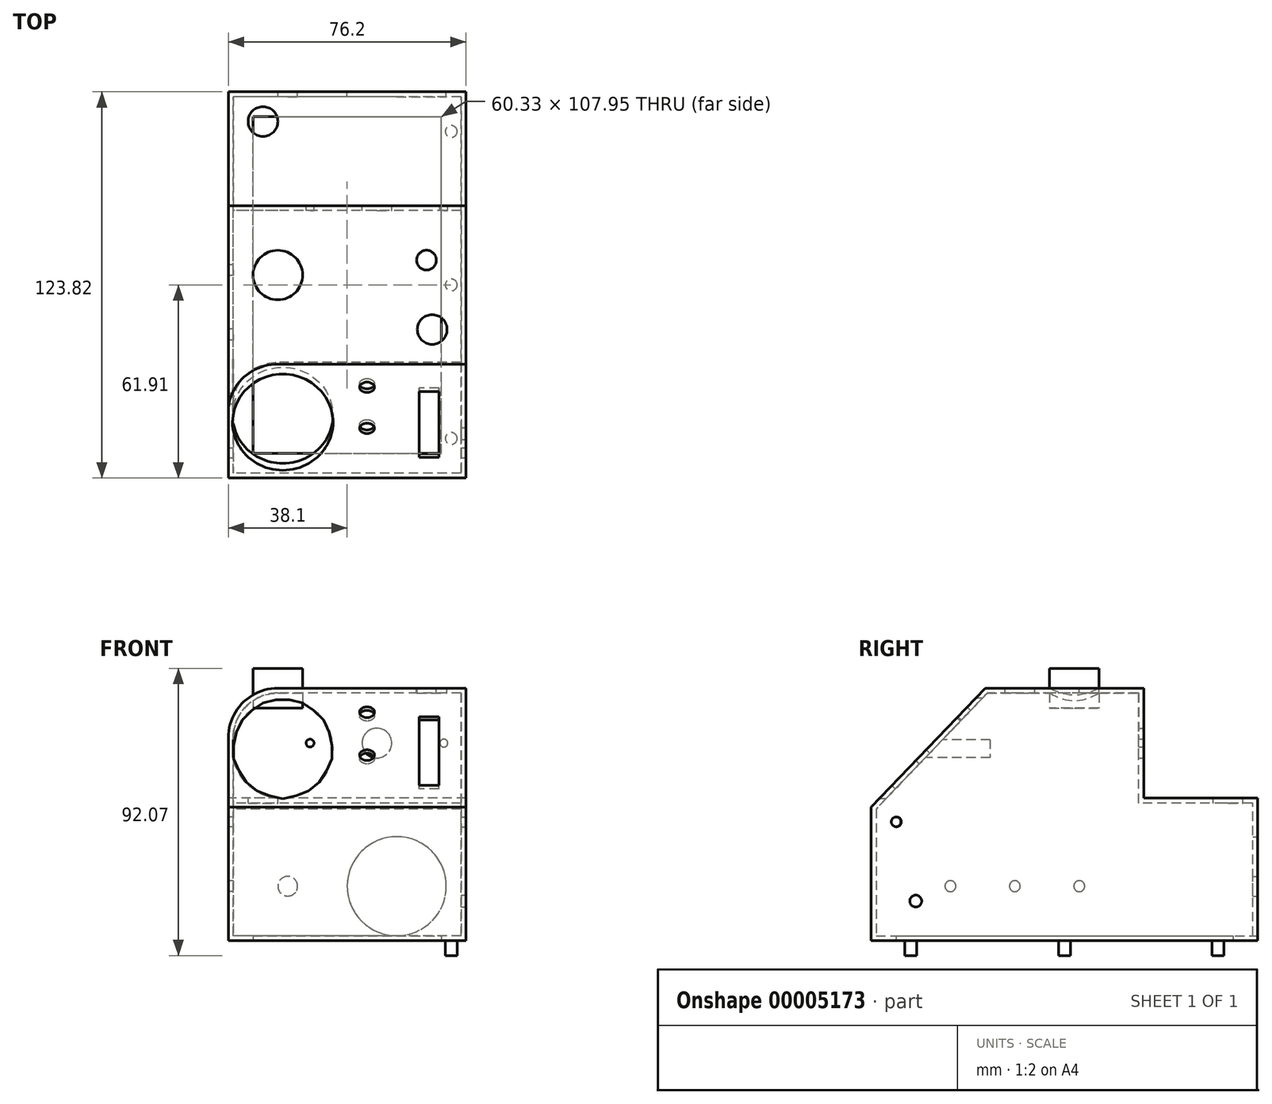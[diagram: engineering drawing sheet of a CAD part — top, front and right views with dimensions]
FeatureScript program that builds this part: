
annotation { "Feature Type Name" : "Feature", "Feature Type Description" : "" }
export const myFeature = defineFeature(function(context is Context, id is Id, definition is map)
    precondition{}
    {
        {
            var Q0;
            Q0=qCreatedBy(makeId("Right.planeOp"),FACE);
            var sketch = newSketch(context, id + "F0", { "sketchPlane" : qUnion([Q0])});
            skLineSegment(sketch, "E0", {"start": v(-61.91, -42.86) * mm, "end": v(61.91, -42.86) * mm});
            skLineSegment(sketch, "E1", {"start": v(61.91, -42.86) * mm, "end": v(61.91, 7.62) * mm});
            skLineSegment(sketch, "E2", {"start": v(61.91, 7.62) * mm, "end": v(25.4, 7.62) * mm});
            skLineSegment(sketch, "E3", {"start": v(25.4, 7.62) * mm, "end": v(25.4, 42.86) * mm});
            skLineSegment(sketch, "E4", {"start": v(25.4, 42.86) * mm, "end": v(-25.4, 42.86) * mm});
            skLineSegment(sketch, "E5", {"start": v(-25.4, 42.86) * mm, "end": v(-61.91, 4.76) * mm});
            skLineSegment(sketch, "E6", {"start": v(-61.91, 4.76) * mm, "end": v(-61.91, -42.86) * mm});
            skLineSegment(sketch, "E7", {"start": v(0, -42.86) * mm, "end": v(0, 42.86) * mm});
            skSolve(sketch);
        }
        {
            var Q0;
            {var subQ5=sQuery(id+"F0.wireOp",EDGE,"E5");var subQ9=sQuery(id+"F0.wireOp",EDGE,"E1");Q0=qUnion([makeQuery(id+"F0.imprint","IMPRINT",FACE,{"disambiguationData":[TD([[makeQuery(id+"F0.imprint","IMPRINT",EDGE,{"derivedFrom":subQ5}),1.0]])]}),makeQuery(id+"F0.imprint","IMPRINT",FACE,{"disambiguationData":[TD([[makeQuery(id+"F0.imprint","IMPRINT",EDGE,{"derivedFrom":subQ9}),1.0]])]})]);}
            extrude(context, id + "F1", {"entities" : qUnion([Q0]), "depth" : 76.2 * mm, "symmetric" : true});
        }
        {
            var Q0;
            Q0=makeQuery(id+"F1.opExtrude","CAP_EDGE",EDGE,{"disambiguationData":[OSD([sQuery(id+"F0.wireOp",EDGE,"E4")])],"isStart":true});
            fillet(context, id + "F2", {"entities" : qUnion([Q0]), "radius" : 15.88 * mm, "tangentPropagation" : true, "allowEdgeOverflow" : false});
        }
        {
            var Q0;
            Q0=makeQuery(id+"F1.opExtrude","SWEPT_FACE",FACE,{"disambiguationData":[OSD([sQuery(id+"F0.wireOp",EDGE,"E0")])]});
            shell(context, id + "F3", {"entities" : qUnion([Q0]), "thickness" : 1.59 * mm});
        }
        {
            var Q0;
            Q0=makeQuery(id+"F1.opExtrude","CAP_FACE",FACE,{"disambiguationData":[OSD([sQuery(id+"F0.wireOp",EDGE,"E0"),sQuery(id+"F0.wireOp",EDGE,"E1"),sQuery(id+"F0.wireOp",EDGE,"E2"),sQuery(id+"F0.wireOp",EDGE,"E3"),sQuery(id+"F0.wireOp",EDGE,"E4"),sQuery(id+"F0.wireOp",EDGE,"E5"),sQuery(id+"F0.wireOp",EDGE,"E6")])],"isStart":true});
            var sketch = newSketch(context, id + "F4", { "sketchPlane" : qUnion([Q0])});
            skCircle(sketch, "E8", {"center": v(36.51, -20.64) * mm, "radius": 1.75 * mm});
            skCircle(sketch, "E9", {"center": v(15.87, -20.64) * mm, "radius": 1.75 * mm});
            skCircle(sketch, "E10", {"center": v(-4.76, -20.64) * mm, "radius": 1.75 * mm});
            skCircle(sketch, "E11", {"center": v(53.97, 0) * mm, "radius": 1.59 * mm});
            skSolve(sketch);
        }
        {
            var Q0;
            {Q0=qUnion([makeQuery(id+"F4.imprint","IMPRINT",FACE,{"disambiguationData":[TD([[makeQuery(id+"F4.imprint","IMPRINT",EDGE,{"derivedFrom":sQuery(id+"F4.wireOp",EDGE,"E8")}),1.0]])]}),makeQuery(id+"F4.imprint","IMPRINT",FACE,{"disambiguationData":[TD([[makeQuery(id+"F4.imprint","IMPRINT",EDGE,{"derivedFrom":sQuery(id+"F4.wireOp",EDGE,"E9")}),1.0]])]}),makeQuery(id+"F4.imprint","IMPRINT",FACE,{"disambiguationData":[TD([[makeQuery(id+"F4.imprint","IMPRINT",EDGE,{"derivedFrom":sQuery(id+"F4.wireOp",EDGE,"E10")}),1.0]])]}),makeQuery(id+"F4.imprint","IMPRINT",FACE,{"disambiguationData":[TD([[makeQuery(id+"F4.imprint","IMPRINT",EDGE,{"derivedFrom":sQuery(id+"F4.wireOp",EDGE,"E11")}),1.0]])]})]);}
            extrude(context, id + "F5", {"entities" : qUnion([Q0]), "operationType" : NewBodyOperationType.REMOVE, "oppositeDirection" : true, "depth" : 25.4 * mm});
        }
        {
            var Q0;
            Q0=makeQuery(id+"F1.opExtrude","CAP_FACE",FACE,{"disambiguationData":[OSD([sQuery(id+"F0.wireOp",EDGE,"E0"),sQuery(id+"F0.wireOp",EDGE,"E1"),sQuery(id+"F0.wireOp",EDGE,"E2"),sQuery(id+"F0.wireOp",EDGE,"E3"),sQuery(id+"F0.wireOp",EDGE,"E4"),sQuery(id+"F0.wireOp",EDGE,"E5"),sQuery(id+"F0.wireOp",EDGE,"E6")])],"isStart":false});
            var sketch = newSketch(context, id + "F6", { "sketchPlane" : qUnion([Q0])});
            skCircle(sketch, "E12", {"center": v(-53.85, 0) * mm, "radius": 1.59 * mm});
            skCircle(sketch, "E13", {"center": v(-47.62, -25.4) * mm, "radius": 1.9 * mm});
            skSolve(sketch);
        }
        {
            var Q0;
            {Q0=qUnion([makeQuery(id+"F6.imprint","IMPRINT",FACE,{"disambiguationData":[TD([[makeQuery(id+"F6.imprint","IMPRINT",EDGE,{"derivedFrom":sQuery(id+"F6.wireOp",EDGE,"E12")}),1.0]])]}),makeQuery(id+"F6.imprint","IMPRINT",FACE,{"disambiguationData":[TD([[makeQuery(id+"F6.imprint","IMPRINT",EDGE,{"derivedFrom":sQuery(id+"F6.wireOp",EDGE,"E13")}),1.0]])]})]);}
            extrude(context, id + "F7", {"entities" : qUnion([Q0]), "operationType" : NewBodyOperationType.REMOVE, "oppositeDirection" : true, "depth" : 25.4 * mm});
        }
        {
            var Q0;
            Q0=makeQuery(id+"F1.opExtrude","SWEPT_FACE",FACE,{"disambiguationData":[OSD([sQuery(id+"F0.wireOp",EDGE,"E0")])]});
            var sketch = newSketch(context, id + "F8", { "sketchPlane" : qUnion([Q0])});
            skLineSegment(sketch, "E14.bottom", {"start": v(-36.51, 60.32) * mm, "end": v(36.51, 60.32) * mm});
            skLineSegment(sketch, "E14.top", {"start": v(-36.51, -60.32) * mm, "end": v(36.51, -60.32) * mm});
            skLineSegment(sketch, "E14.left", {"start": v(-36.51, 60.32) * mm, "end": v(-36.51, -60.32) * mm});
            skLineSegment(sketch, "E14.right", {"start": v(36.51, 60.32) * mm, "end": v(36.51, -60.32) * mm});
            skLineSegment(sketch, "E15.0", {"start": v(-30.16, 53.97) * mm, "end": v(30.16, 53.97) * mm});
            skLineSegment(sketch, "E15.1", {"start": v(-30.16, 53.97) * mm, "end": v(-30.16, -53.97) * mm});
            skLineSegment(sketch, "E15.2", {"start": v(-30.16, -53.97) * mm, "end": v(30.16, -53.97) * mm});
            skLineSegment(sketch, "E15.3", {"start": v(30.16, 53.97) * mm, "end": v(30.16, -53.97) * mm});
            skSolve(sketch);
        }
        {
            var Q0;
            Q0=makeQuery(id+"F8.imprint","IMPRINT",FACE,{"disambiguationData":[TD([[makeQuery(id+"F8.imprint","IMPRINT",EDGE,{"derivedFrom":sQuery(id+"F8.wireOp",EDGE,"E14.bottom")}),1.0]])]});
            extrude(context, id + "F9", {"entities" : qUnion([Q0]), "operationType" : NewBodyOperationType.ADD, "oppositeDirection" : true, "depth" : 6.35 * mm});
        }
        {
            var Q0;
            Q0=makeQuery(id+"F9.boolean.opBoolean","MERGE",FACE,{"derivedFrom":[makeQuery(id+"F1.opExtrude","SWEPT_FACE",FACE,{"disambiguationData":[OSD([sQuery(id+"F0.wireOp",EDGE,"E0")])]}),makeQuery(id+"F9.opExtrude","CAP_FACE",FACE,{"disambiguationData":[OSD([sQuery(id+"F8.wireOp",EDGE,"E14.bottom"),sQuery(id+"F8.wireOp",EDGE,"E14.top"),sQuery(id+"F8.wireOp",EDGE,"E14.left"),sQuery(id+"F8.wireOp",EDGE,"E14.right"),sQuery(id+"F8.wireOp",EDGE,"E15.0"),sQuery(id+"F8.wireOp",EDGE,"E15.1"),sQuery(id+"F8.wireOp",EDGE,"E15.2"),sQuery(id+"F8.wireOp",EDGE,"E15.3")])],"isStart":true})]});
            var sketch = newSketch(context, id + "F10", { "sketchPlane" : qUnion([Q0])});
            skCircle(sketch, "E16", {"center": v(-33.34, 49.21) * mm, "radius": 1.9 * mm});
            skCircle(sketch, "E17", {"center": v(-33.34, 0) * mm, "radius": 1.9 * mm});
            skCircle(sketch, "E18", {"center": v(-33.34, -49.21) * mm, "radius": 1.9 * mm});
            skCircle(sketch, "E19.0.MirrorC", {"center": v(33.34, -49.21) * mm, "radius": 1.9 * mm});
            skCircle(sketch, "E19.1.MirrorC", {"center": v(33.34, 0) * mm, "radius": 1.9 * mm});
            skCircle(sketch, "E19.2.MirrorC", {"center": v(33.34, 49.21) * mm, "radius": 1.9 * mm});
            skSolve(sketch);
        }
        {
            var Q0;
            {Q0=qUnion([makeQuery(id+"F10.imprint","IMPRINT",FACE,{"disambiguationData":[TD([[makeQuery(id+"F10.imprint","IMPRINT",EDGE,{"derivedFrom":sQuery(id+"F10.wireOp",EDGE,"E16")}),1.0]])]}),makeQuery(id+"F10.imprint","IMPRINT",FACE,{"disambiguationData":[TD([[makeQuery(id+"F10.imprint","IMPRINT",EDGE,{"derivedFrom":sQuery(id+"F10.wireOp",EDGE,"E17")}),1.0]])]}),makeQuery(id+"F10.imprint","IMPRINT",FACE,{"disambiguationData":[TD([[makeQuery(id+"F10.imprint","IMPRINT",EDGE,{"derivedFrom":sQuery(id+"F10.wireOp",EDGE,"E18")}),1.0]])]}),makeQuery(id+"F10.imprint","IMPRINT",FACE,{"disambiguationData":[TD([[makeQuery(id+"F10.imprint","IMPRINT",EDGE,{"derivedFrom":sQuery(id+"F10.wireOp",EDGE,"E19.0.MirrorC")}),-1.0]])]}),makeQuery(id+"F10.imprint","IMPRINT",FACE,{"disambiguationData":[TD([[makeQuery(id+"F10.imprint","IMPRINT",EDGE,{"derivedFrom":sQuery(id+"F10.wireOp",EDGE,"E19.1.MirrorC")}),-1.0]])]}),makeQuery(id+"F10.imprint","IMPRINT",FACE,{"disambiguationData":[TD([[makeQuery(id+"F10.imprint","IMPRINT",EDGE,{"derivedFrom":sQuery(id+"F10.wireOp",EDGE,"E19.2.MirrorC")}),-1.0]])]})]);}
            extrude(context, id + "F11", {"entities" : qUnion([Q0]), "operationType" : NewBodyOperationType.REMOVE, "oppositeDirection" : true, "depth" : 4.76 * mm});
        }
        {
            var Q0;
            Q0=makeQuery(id+"F1.opExtrude","SWEPT_FACE",FACE,{"disambiguationData":[OSD([sQuery(id+"F0.wireOp",EDGE,"E1")])]});
            var sketch = newSketch(context, id + "F12", { "sketchPlane" : qUnion([Q0])});
            skCircle(sketch, "E20", {"center": v(-15.88, -20.64) * mm, "radius": 15.88 * mm});
            skCircle(sketch, "E21", {"center": v(19.05, -20.64) * mm, "radius": 3.18 * mm});
            skSolve(sketch);
        }
        {
            var Q0;
            {Q0=qUnion([makeQuery(id+"F12.imprint","IMPRINT",FACE,{"disambiguationData":[TD([[makeQuery(id+"F12.imprint","IMPRINT",EDGE,{"derivedFrom":sQuery(id+"F12.wireOp",EDGE,"E20")}),1.0]])]}),makeQuery(id+"F12.imprint","IMPRINT",FACE,{"disambiguationData":[TD([[makeQuery(id+"F12.imprint","IMPRINT",EDGE,{"derivedFrom":sQuery(id+"F12.wireOp",EDGE,"E21")}),1.0]])]})]);}
            extrude(context, id + "F13", {"entities" : qUnion([Q0]), "operationType" : NewBodyOperationType.REMOVE, "oppositeDirection" : true, "depth" : 25.4 * mm});
        }
        {
            var Q0;
            Q0=makeQuery(id+"F1.opExtrude","SWEPT_FACE",FACE,{"disambiguationData":[OSD([sQuery(id+"F0.wireOp",EDGE,"E3")])]});
            var sketch = newSketch(context, id + "F14", { "sketchPlane" : qUnion([Q0])});
            skCircle(sketch, "E22", {"center": v(-30.96, 25.24) * mm, "radius": 1.27 * mm});
            skCircle(sketch, "E23", {"center": v(-9.52, 25.24) * mm, "radius": 4.76 * mm});
            skCircle(sketch, "E24", {"center": v(11.9, 25.24) * mm, "radius": 1.27 * mm});
            skLineSegment(sketch, "E25", {"start": v(-0.96, 42.86) * mm, "end": v(-0.96, 7.62) * mm, "construction": true});
            skPoint(sketch, "E26", {"position": v(-0.96, 25.24) * mm});
            skSolve(sketch);
        }
        {
            var Q0;
            {Q0=qUnion([makeQuery(id+"F14.imprint","IMPRINT",FACE,{"disambiguationData":[TD([[makeQuery(id+"F14.imprint","IMPRINT",EDGE,{"derivedFrom":sQuery(id+"F14.wireOp",EDGE,"E22")}),1.0]])]}),makeQuery(id+"F14.imprint","IMPRINT",FACE,{"disambiguationData":[TD([[makeQuery(id+"F14.imprint","IMPRINT",EDGE,{"derivedFrom":sQuery(id+"F14.wireOp",EDGE,"E23")}),1.0]])]}),makeQuery(id+"F14.imprint","IMPRINT",FACE,{"disambiguationData":[TD([[makeQuery(id+"F14.imprint","IMPRINT",EDGE,{"derivedFrom":sQuery(id+"F14.wireOp",EDGE,"E24")}),1.0]])]})]);}
            extrude(context, id + "F15", {"entities" : qUnion([Q0]), "operationType" : NewBodyOperationType.REMOVE, "oppositeDirection" : true, "depth" : 25.4 * mm});
        }
        {
            var Q0;
            Q0=makeQuery(id+"F1.opExtrude","SWEPT_FACE",FACE,{"disambiguationData":[OSD([sQuery(id+"F0.wireOp",EDGE,"E5")])]});
            var sketch = newSketch(context, id + "F16", { "sketchPlane" : qUnion([Q0])});
            skCircle(sketch, "E27", {"center": v(6.35, 2.67) * mm, "radius": 2.38 * mm});
            skCircle(sketch, "E28", {"center": v(6.35, -16.38) * mm, "radius": 2.38 * mm});
            skLineSegment(sketch, "E29.bottom", {"start": v(23.01, 0.67) * mm, "end": v(29.36, 0.67) * mm});
            skLineSegment(sketch, "E29.top", {"start": v(23.01, -29.87) * mm, "end": v(29.36, -29.87) * mm});
            skLineSegment(sketch, "E29.left", {"start": v(23.01, 0.67) * mm, "end": v(23.01, -29.87) * mm});
            skLineSegment(sketch, "E29.right", {"start": v(29.36, 0.67) * mm, "end": v(29.36, -29.87) * mm});
            skSolve(sketch);
        }
        {
            var Q0;
            {Q0=qUnion([makeQuery(id+"F16.imprint","IMPRINT",FACE,{"disambiguationData":[TD([[makeQuery(id+"F16.imprint","IMPRINT",EDGE,{"derivedFrom":sQuery(id+"F16.wireOp",EDGE,"E27")}),1.0]])]}),makeQuery(id+"F16.imprint","IMPRINT",FACE,{"disambiguationData":[TD([[makeQuery(id+"F16.imprint","IMPRINT",EDGE,{"derivedFrom":sQuery(id+"F16.wireOp",EDGE,"E28")}),1.0]])]}),makeQuery(id+"F16.imprint","IMPRINT",FACE,{"disambiguationData":[TD([[makeQuery(id+"F16.imprint","IMPRINT",EDGE,{"derivedFrom":sQuery(id+"F16.wireOp",EDGE,"E29.bottom")}),-1.0]])]})]);}
            extrude(context, id + "F17", {"entities" : qUnion([Q0]), "operationType" : NewBodyOperationType.REMOVE, "oppositeDirection" : true, "depth" : 25.4 * mm});
        }
        {
            var Q0;
            Q0=makeQuery(id+"F1.opExtrude","SWEPT_FACE",FACE,{"disambiguationData":[OSD([sQuery(id+"F0.wireOp",EDGE,"E4")])]});
            var sketch = newSketch(context, id + "F18", { "sketchPlane" : qUnion([Q0])});
            skCircle(sketch, "E30", {"center": v(27.23, -14.29) * mm, "radius": 4.76 * mm});
            skCircle(sketch, "E31", {"center": v(25.4, 7.94) * mm, "radius": 3.18 * mm});
            skSolve(sketch);
        }
        {
            var Q0;
            Q0=makeQuery(id+"F18.imprint","IMPRINT",FACE,{"disambiguationData":[TD([[makeQuery(id+"F18.imprint","IMPRINT",EDGE,{"derivedFrom":sQuery(id+"F18.wireOp",EDGE,"E31")}),1.0]])]});
            var Q1;
            Q1=makeQuery(id+"F18.imprint","IMPRINT",FACE,{"disambiguationData":[TD([[makeQuery(id+"F18.imprint","IMPRINT",EDGE,{"derivedFrom":sQuery(id+"F18.wireOp",EDGE,"E30")}),1.0]])]});
            extrude(context, id + "F19", {"entities" : qUnion([Q0, Q1]), "operationType" : NewBodyOperationType.REMOVE, "oppositeDirection" : true, "depth" : 25.4 * mm});
        }
        {
            var Q0;
            Q0=makeQuery(id+"F1.opExtrude","SWEPT_FACE",FACE,{"disambiguationData":[OSD([sQuery(id+"F0.wireOp",EDGE,"E2")])]});
            var sketch = newSketch(context, id + "F20", { "sketchPlane" : qUnion([Q0])});
            skCircle(sketch, "E32", {"center": v(-26.99, 52.39) * mm, "radius": 4.76 * mm});
            skSolve(sketch);
        }
        {
            var Q0;
            Q0=makeQuery(id+"F20.imprint","IMPRINT",FACE,{"disambiguationData":[TD([[makeQuery(id+"F20.imprint","IMPRINT",EDGE,{"derivedFrom":sQuery(id+"F20.wireOp",EDGE,"E32")}),1.0]])]});
            extrude(context, id + "F21", {"entities" : qUnion([Q0]), "operationType" : NewBodyOperationType.REMOVE, "oppositeDirection" : true, "depth" : 25.4 * mm});
        }
        {
            var Q0;
            Q0=makeQuery(id+"F18.imprint","IMPRINT",FACE,{"disambiguationData":[TD([[makeQuery(id+"F18.imprint","IMPRINT",EDGE,{"derivedFrom":sQuery(id+"F18.wireOp",EDGE,"E30")}),-1.0]])]});
            var sketch = newSketch(context, id + "F22", { "sketchPlane" : qUnion([Q0])});
            skCircle(sketch, "E33", {"center": v(-22.23, 3.18) * mm, "radius": 7.94 * mm});
            skSolve(sketch);
        }
        {
            var Q0;
            Q0 = qSketchRegion(id + "F22", true);
            extrude(context, id + "F23", {"entities" : qUnion([Q0]), "operationType" : NewBodyOperationType.ADD, "depth" : 12.7 * mm, "symmetric" : true});
        }
        {
            var Q0;
            Q0=makeQuery(id+"F1.opExtrude","SWEPT_FACE",FACE,{"disambiguationData":[OSD([sQuery(id+"F0.wireOp",EDGE,"E6")])]});
            var sketch = newSketch(context, id + "F24", { "sketchPlane" : qUnion([Q0])});
            skCircle(sketch, "E34", {"center": v(-20.64, 23.5) * mm, "radius": 16.13 * mm});
            skSolve(sketch);
        }
        {
            var Q0;
            Q0=makeQuery(id+"F24.imprint","IMPRINT",FACE,{"disambiguationData":[TD([[makeQuery(id+"F24.imprint","IMPRINT",EDGE,{"derivedFrom":sQuery(id+"F24.wireOp",EDGE,"E34")}),1.0]])]});
            extrude(context, id + "F25", {"entities" : qUnion([Q0]), "operationType" : NewBodyOperationType.REMOVE, "oppositeDirection" : true, "depth" : 38.1 * mm});
        }
    });
